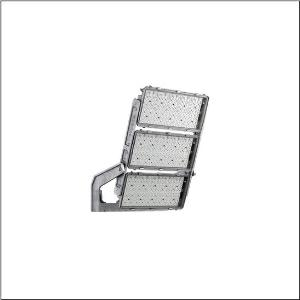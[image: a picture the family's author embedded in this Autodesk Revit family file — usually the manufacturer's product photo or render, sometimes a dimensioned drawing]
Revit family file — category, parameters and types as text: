
# Revit family: floodlight_fl_11_maxi_pro_remote___pl64blc_5xa779425w01aa_643d
name_source: partatom
category: Lighting Fixtures
units: mm (PartAtom-declared; Revit-internal decimal feet)

## family parameters
Cut with Voids When Loaded = No
Host = Face
Light Source = No
Part Type = Normal
Room Calculation Point = No
Round Connector Dimension = Use Diameter
Shared = No

## types (1)
- --- (1 x LED, 135060 lm, 1516.7 W, 3000K)
    Apparent Load = 1517 VA
    CIE Flux Codes = 28 83 99 100 100
    Color Rendering = 70
    Color Temperature = 3000K
    Default Elevation = 1800 mm
    Description = Floodlight FL 11  maxi  pro Remote floodlight; light control with lens of PMMA; cover panel of toughened safety glass, transparent; light distribution: PL64BLC, asymmetric direct distribution, LEDcolour temperature: 3000K, rated luminous flux: 135.060lm, colour rendering: CRI > 70, light colour: 730; luminous efficacy: 89lm/W; brightness control: DALI 2 (1 DALI address); with terminal, 8-pole, max. 2.5mm², mains connection: 220..240V/380..400V AC, 50/60Hz, surge voltage resistance: line to ground: 10kV, ECG replaceable separately, no afterglow with DALI off / DMX off command, LED unit replaceable without ESD environment, dustproof LED module, dimming range 10..100%; 1517W floodlight with 2x LED unit of diecast aluminium, coated grey; length: 713mm / width: 651mm / height: 338mm; mounting bracket, of diecast aluminium, uncoated, natural, equipment: Power, protection rating (complete): IP66; insulation class (complete): insulation class I (protective earthing); certification: CE, ENEC, VDE; ball protection: ball impact resistance with accessories, impact resistance: IK07; only for outdoor installations, rated ambient temperature 10°C, permissible operating ambient temperature: -40..+30°C, permissible storage temperature: -40..+85°C; packaging unit: 1 piece

Light Distribution: PL64BLC
    Height = 320 mm
    Lamp = 1 x LED
    Lamp Light Flux = 135060 lm
    Lamp Power = 1516.7 W
    Lamp count = 1
    Length = 1002 mm
    Luminous efficacy = 89 lm/W
    Manufacturer = Siteco
    ModVariant = No
    Model = 5XA779425W01AA
    Mounting Place = Ceiling
    Mounting Type = Surface mounted
    Number of Poles = 1
    OnlyDefault = Yes
    Power Factor = 1
    Product Name = Floodlight FL 11 maxi pro Remote | PL64BLC
    Product group = floodlight | ceiling mounted
    ProductGroupID = 303
    Protection Class = Protection class I
    Protection Degree = IP 66
    RLX_Detail_Level = 1
    RLX_Emergency_Light_Flux = 0 lm
    RLX_Emergency_Type = 0
    RLX_Emergency_Type_DB = No
    RlxData = <blob elided: 52153 chars, md5=686edb30>
    Socket = socket
    Standby Power = 0 W
    System Light Flux = 135060 lm
    System Power = 1517 W
    Type Comments = factory setting: luminous flux: 100 % | dim-lin: 254 | 1070 mA
    Type Image = l_1006784.jpg
    URL = http://relux.com
    VarID = @adj_033045
    Voltage = 0 V
    Weight = 0.00 kg
    Width = 655 mm

## geometry (parser evidence)
native form markers: Blend x4, Sweep x13
no freeform markers — native parametric forms only
